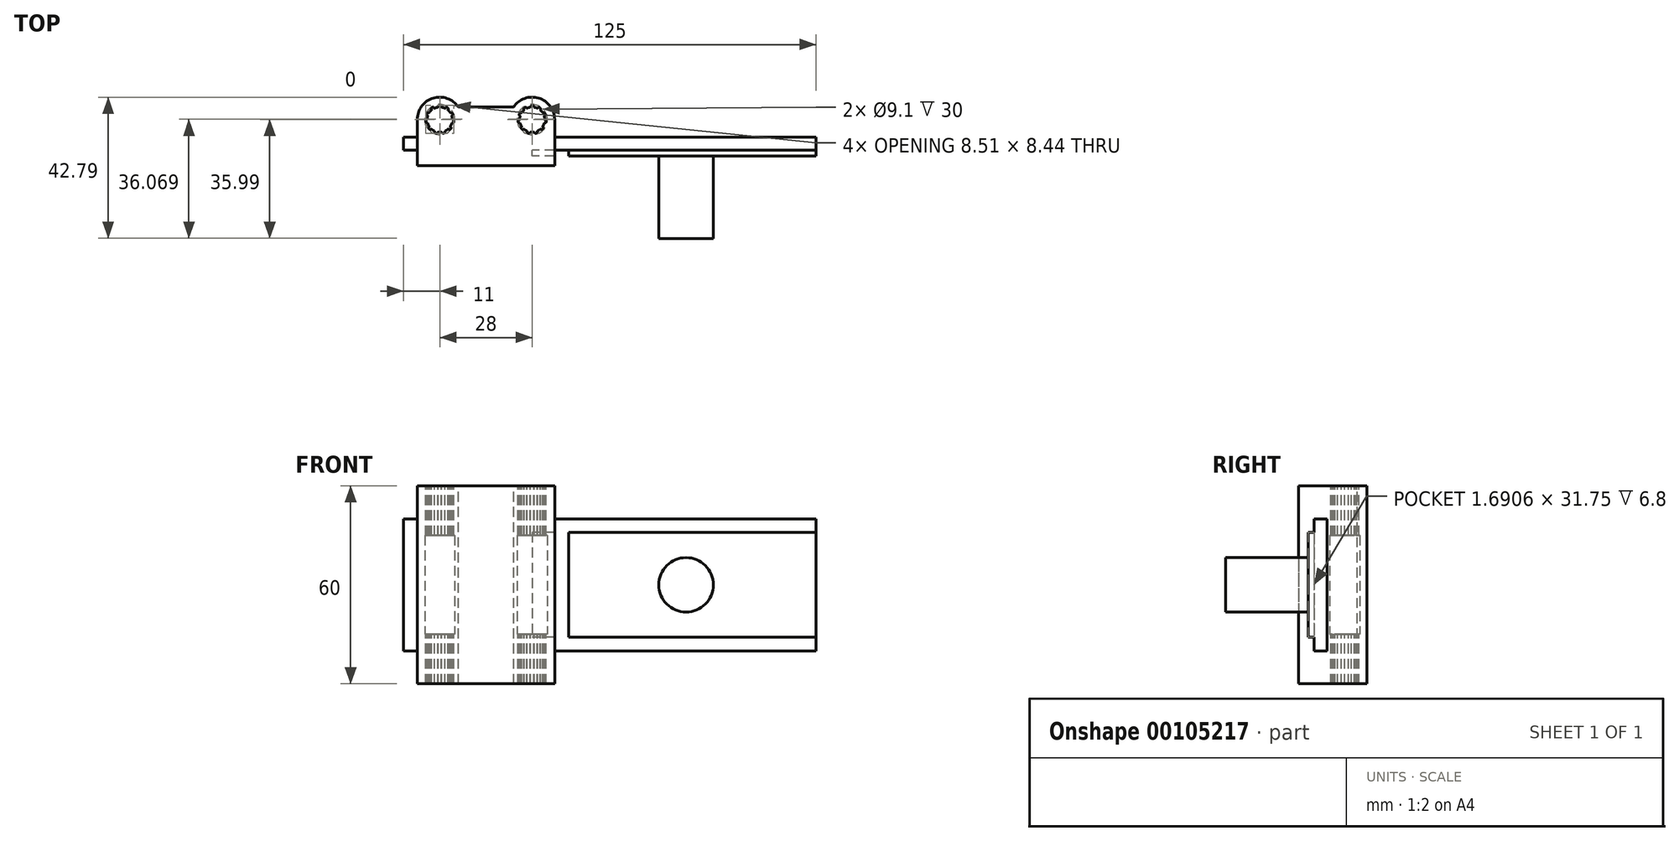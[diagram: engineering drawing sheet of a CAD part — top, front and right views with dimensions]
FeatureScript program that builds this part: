
annotation { "Feature Type Name" : "Feature", "Feature Type Description" : "" }
export const myFeature = defineFeature(function(context is Context, id is Id, definition is map)
    precondition{}
    {
        {
            assignVariable(context, id + "F0", {"name" : "tubeSpacing", "anyValue" : 28});
        }
        {
            var Q0;
            Q0=qCreatedBy(makeId("Right.planeOp"),FACE);
            var sketch = newSketch(context, id + "F1", { "sketchPlane" : qUnion([Q0])});
            skLineSegment(sketch, "E0.bottom", {"start": v(2, 20) * mm, "end": v(-2, 20) * mm});
            skLineSegment(sketch, "E0.top", {"start": v(2, -20) * mm, "end": v(-2, -20) * mm});
            skLineSegment(sketch, "E0.left", {"start": v(2, 20) * mm, "end": v(2, -20) * mm});
            skLineSegment(sketch, "E0.right", {"start": v(-2, 20) * mm, "end": v(-2, -20) * mm});
            skPoint(sketch, "E0.middle", {"position": v(0, 0) * mm});
            skLineSegment(sketch, "E1.bottom", {"start": v(-6, -28) * mm, "end": v(-2, -28) * mm});
            skLineSegment(sketch, "E1.top", {"start": v(-6, 28) * mm, "end": v(-2, 28) * mm});
            skLineSegment(sketch, "E1.left", {"start": v(-6, -28) * mm, "end": v(-6, 28) * mm});
            skPoint(sketch, "E1.middle", {"position": v(-4, 0) * mm});
            skLineSegment(sketch, "E2.bottom", {"start": v(6, -28) * mm, "end": v(2, -28) * mm});
            skLineSegment(sketch, "E2.top", {"start": v(6, 28) * mm, "end": v(2, 28) * mm});
            skLineSegment(sketch, "E2.left", {"start": v(6, -28) * mm, "end": v(6, 28) * mm});
            skPoint(sketch, "E2.middle", {"position": v(4, 0) * mm});
            skLineSegment(sketch, "E3", {"start": v(-2, 28) * mm, "end": v(2, 28) * mm});
            skLineSegment(sketch, "E4", {"start": v(-2, -28) * mm, "end": v(2, -28) * mm});
            skLineSegment(sketch, "E5", {"start": v(-2, 20) * mm, "end": v(-2, 28) * mm});
            skLineSegment(sketch, "E6", {"start": v(2, 20) * mm, "end": v(2, 28) * mm});
            skLineSegment(sketch, "E7", {"start": v(2, -20) * mm, "end": v(2, -28) * mm});
            skLineSegment(sketch, "E8", {"start": v(-2, -20) * mm, "end": v(-2, -28) * mm});
            skPoint(sketch, "E9", {"position": v(0, 24) * mm});
            skPoint(sketch, "E9.positionSnap0", {"position": v(-2, 24) * mm});
            skPoint(sketch, "E9.positionSnap1", {"position": v(0, 20) * mm});
            skPoint(sketch, "E10", {"position": v(0, -24) * mm});
            skLineSegment(sketch, "E11.bottom", {"start": v(-2.5, -15.88) * mm, "end": v(-3.7, -15.88) * mm});
            skLineSegment(sketch, "E11.top", {"start": v(-2.5, 15.88) * mm, "end": v(-3.7, 15.88) * mm});
            skLineSegment(sketch, "E11.left", {"start": v(-2.5, -15.88) * mm, "end": v(-2.5, 15.88) * mm});
            skLineSegment(sketch, "E11.right", {"start": v(-3.7, -15.88) * mm, "end": v(-3.7, 15.88) * mm});
            skPoint(sketch, "E11.middle", {"position": v(-3.1, 0) * mm});
            skLineSegment(sketch, "E12", {"start": v(-2.5, 15.88) * mm, "end": v(-2, 15.88) * mm});
            skLineSegment(sketch, "E13", {"start": v(-2.5, -15.88) * mm, "end": v(-2, -15.88) * mm});
            skSolve(sketch);
        }
        {
            var Q0;
            {var subQ1=sQuery(id+"F1.wireOp",EDGE,"E0.bottom");Q0=makeQuery(id+"F1.imprint","IMPRINT",FACE,{"disambiguationData":[TD([[makeQuery(id+"F1.imprint","IMPRINT",EDGE,{"derivedFrom":subQ1}),1.0]])]});}
            extrude(context, id + "F2", {"entities" : qUnion([Q0]), "oppositeDirection" : true, "depth" : 25 * mm, "hasSecondDirection" : true, "secondDirectionOppositeDirection" : false, "secondDirectionDepth" : 100 * mm});
        }
        {
            var Q0;
            Q0=makeQuery(id+"F1.imprint","IMPRINT",FACE,{"disambiguationData":[TD([[makeQuery(id+"F1.imprint","IMPRINT",EDGE,{"derivedFrom":sQuery(id+"F1.wireOp",EDGE,"E11.bottom")}),-1.0]])]});
            var Q1;
            Q1=makeQuery(id+"F1.imprint","IMPRINT",FACE,{"disambiguationData":[TD([[makeQuery(id+"F1.imprint","IMPRINT",EDGE,{"derivedFrom":sQuery(id+"F1.wireOp",EDGE,"E11.left")}),-1.0]])]});
            extrude(context, id + "F3", {"entities" : qUnion([Q0, Q1]), "operationType" : NewBodyOperationType.ADD, "depth" : 100 * mm, "hasSecondDirection" : true, "secondDirectionOppositeDirection" : false, "secondDirectionDepth" : (getVariable(context, 'tubeSpacing') / 2) * mm});
        }
        {
            var Q0;
            Q0=qCreatedBy(makeId("Top.planeOp"),FACE);
            var sketch = newSketch(context, id + "F4", { "sketchPlane" : qUnion([Q0])});
            skArc(sketch, "E14", {"start": v(-16.46, 10.2) * mm, "mid": v(-16.87, 9.79) * mm, "end": v(-17.22, 9.32) * mm});
            skLineSegment(sketch, "E15", {"start": v(-14, 7.3) * mm, "end": v(14, 7.3) * mm, "construction": true});
            skPoint(sketch, "E16", {"position": v(0, 7.3) * mm});
            skArc(sketch, "E17", {"start": v(-9.74, 2) * mm, "mid": v(-11.06, 13.43) * mm, "end": v(-20.8, 7.3) * mm});
            skArc(sketch, "E18", {"start": v(20.8, 7.3) * mm, "mid": v(11.06, 13.43) * mm, "end": v(9.74, 2) * mm});
            skLineSegment(sketch, "E19.0.0", {"start": v(100, -2) * mm, "end": v(100, 2) * mm});
            skLineSegment(sketch, "E19.0.1", {"start": v(100, 2) * mm, "end": v(-25, 2) * mm});
            skLineSegment(sketch, "E19.0.2", {"start": v(-25, 2) * mm, "end": v(-25, -2) * mm});
            skLineSegment(sketch, "E19.0.3", {"start": v(-25, -2) * mm, "end": v(100, -2) * mm});
            skLineSegment(sketch, "E20", {"start": v(-14, 11.1) * mm, "end": v(-8.36, 11.1) * mm, "construction": true});
            skLineSegment(sketch, "E21", {"start": v(-8.36, 11.1) * mm, "end": v(8.36, 11.1) * mm});
            skLineSegment(sketch, "E22", {"start": v(8.36, 11.1) * mm, "end": v(14, 11.1) * mm, "construction": true});
            skLineSegment(sketch, "E23", {"start": v(-20.8, 2) * mm, "end": v(-20.8, 7.3) * mm});
            skLineSegment(sketch, "E24", {"start": v(0, 7.3) * mm, "end": v(0, 0) * mm, "construction": true});
            skLineSegment(sketch, "E25.MirrorCS", {"start": v(20.8, 2) * mm, "end": v(20.8, 7.3) * mm});
            skCircle(sketch, "E26", {"center": v(-14, 7.3) * mm, "radius": 4.55 * mm});
            skCircle(sketch, "E27", {"center": v(14, 7.3) * mm, "radius": 4.55 * mm});
            skArc(sketch, "E28", {"start": v(-13.5, 11.07) * mm, "mid": v(-14, 11.6) * mm, "end": v(-14.5, 11.07) * mm});
            skArc(sketch, "E29.1.0", {"start": v(-15.62, 10.74) * mm, "mid": v(-16.32, 10.92) * mm, "end": v(-16.46, 10.2) * mm});
            skArc(sketch, "E29.2.0", {"start": v(-17.22, 9.32) * mm, "mid": v(-17.91, 9.09) * mm, "end": v(-17.63, 8.41) * mm});
            skArc(sketch, "E29.3.0", {"start": v(-17.8, 7.26) * mm, "mid": v(-18.26, 6.69) * mm, "end": v(-17.66, 6.27) * mm});
            skArc(sketch, "E29.4.0", {"start": v(-17.17, 5.21) * mm, "mid": v(-17.25, 4.48) * mm, "end": v(-16.52, 4.46) * mm});
            skArc(sketch, "E29.5.0", {"start": v(-15.54, 3.83) * mm, "mid": v(-15.21, 3.17) * mm, "end": v(-14.58, 3.54) * mm});
            skArc(sketch, "E29.6.0", {"start": v(-13.42, 3.54) * mm, "mid": v(-12.79, 3.17) * mm, "end": v(-12.46, 3.83) * mm});
            skArc(sketch, "E29.7.0", {"start": v(-11.48, 4.46) * mm, "mid": v(-10.75, 4.48) * mm, "end": v(-10.83, 5.21) * mm});
            skArc(sketch, "E29.8.0", {"start": v(-10.34, 6.27) * mm, "mid": v(-9.74, 6.69) * mm, "end": v(-10.2, 7.26) * mm});
            skArc(sketch, "E29.9.0", {"start": v(-10.37, 8.41) * mm, "mid": v(-10.09, 9.09) * mm, "end": v(-10.78, 9.32) * mm});
            skArc(sketch, "E29.10.0", {"start": v(-11.54, 10.2) * mm, "mid": v(-11.68, 10.92) * mm, "end": v(-12.38, 10.74) * mm});
            skArc(sketch, "E30.trimOffspring", {"start": v(-14.5, 11.07) * mm, "mid": v(-15.07, 10.95) * mm, "end": v(-15.62, 10.74) * mm});
            skArc(sketch, "E31.trimOffspring", {"start": v(-12.38, 10.74) * mm, "mid": v(-12.93, 10.95) * mm, "end": v(-13.5, 11.07) * mm});
            skArc(sketch, "E32.trimOffspring", {"start": v(-10.78, 9.32) * mm, "mid": v(-11.13, 9.79) * mm, "end": v(-11.54, 10.2) * mm});
            skArc(sketch, "E33.trimOffspring", {"start": v(-10.2, 7.26) * mm, "mid": v(-10.24, 7.84) * mm, "end": v(-10.37, 8.41) * mm});
            skArc(sketch, "E34.trimOffspring", {"start": v(-10.83, 5.21) * mm, "mid": v(-10.54, 5.72) * mm, "end": v(-10.34, 6.27) * mm});
            skArc(sketch, "E35.trimOffspring", {"start": v(-12.46, 3.83) * mm, "mid": v(-11.95, 4.1) * mm, "end": v(-11.48, 4.46) * mm});
            skArc(sketch, "E36.trimOffspring", {"start": v(-14.58, 3.54) * mm, "mid": v(-14, 3.5) * mm, "end": v(-13.42, 3.54) * mm});
            skArc(sketch, "E37.trimOffspring", {"start": v(-16.52, 4.46) * mm, "mid": v(-16.05, 4.1) * mm, "end": v(-15.54, 3.83) * mm});
            skArc(sketch, "E38.trimOffspring", {"start": v(-17.66, 6.27) * mm, "mid": v(-17.46, 5.72) * mm, "end": v(-17.17, 5.21) * mm});
            skArc(sketch, "E39.trimOffspring", {"start": v(-17.63, 8.41) * mm, "mid": v(-17.76, 7.84) * mm, "end": v(-17.8, 7.26) * mm});
            skArc(sketch, "E40.MirrorCS", {"start": v(13.5, 11.07) * mm, "mid": v(14, 11.6) * mm, "end": v(14.5, 11.07) * mm});
            skArc(sketch, "E41.MirrorCS", {"start": v(12.38, 10.74) * mm, "mid": v(12.93, 10.95) * mm, "end": v(13.5, 11.07) * mm});
            skArc(sketch, "E42.MirrorCS", {"start": v(11.54, 10.2) * mm, "mid": v(11.68, 10.92) * mm, "end": v(12.38, 10.74) * mm});
            skArc(sketch, "E43.MirrorCS", {"start": v(10.78, 9.32) * mm, "mid": v(11.13, 9.79) * mm, "end": v(11.54, 10.2) * mm});
            skArc(sketch, "E44.MirrorCS", {"start": v(10.37, 8.41) * mm, "mid": v(10.09, 9.09) * mm, "end": v(10.78, 9.32) * mm});
            skArc(sketch, "E45.MirrorCS", {"start": v(10.2, 7.26) * mm, "mid": v(10.24, 7.84) * mm, "end": v(10.37, 8.41) * mm});
            skArc(sketch, "E46.MirrorCS", {"start": v(10.34, 6.27) * mm, "mid": v(9.74, 6.69) * mm, "end": v(10.2, 7.26) * mm});
            skArc(sketch, "E47.MirrorCS", {"start": v(10.83, 5.21) * mm, "mid": v(10.54, 5.72) * mm, "end": v(10.34, 6.27) * mm});
            skArc(sketch, "E48.MirrorCS", {"start": v(11.48, 4.46) * mm, "mid": v(10.75, 4.48) * mm, "end": v(10.83, 5.21) * mm});
            skArc(sketch, "E49.MirrorCS", {"start": v(12.46, 3.83) * mm, "mid": v(11.95, 4.1) * mm, "end": v(11.48, 4.46) * mm});
            skArc(sketch, "E50.MirrorCS", {"start": v(13.42, 3.54) * mm, "mid": v(12.79, 3.17) * mm, "end": v(12.46, 3.83) * mm});
            skArc(sketch, "E51.MirrorCS", {"start": v(14.58, 3.54) * mm, "mid": v(14, 3.5) * mm, "end": v(13.42, 3.54) * mm});
            skArc(sketch, "E52.MirrorCS", {"start": v(15.54, 3.83) * mm, "mid": v(15.21, 3.17) * mm, "end": v(14.58, 3.54) * mm});
            skArc(sketch, "E53.MirrorCS", {"start": v(16.52, 4.46) * mm, "mid": v(16.05, 4.1) * mm, "end": v(15.54, 3.83) * mm});
            skArc(sketch, "E54.MirrorCS", {"start": v(17.17, 5.21) * mm, "mid": v(17.25, 4.48) * mm, "end": v(16.52, 4.46) * mm});
            skArc(sketch, "E55.MirrorCS", {"start": v(17.66, 6.27) * mm, "mid": v(17.46, 5.72) * mm, "end": v(17.17, 5.21) * mm});
            skArc(sketch, "E56.MirrorCS", {"start": v(17.8, 7.26) * mm, "mid": v(18.26, 6.69) * mm, "end": v(17.66, 6.27) * mm});
            skArc(sketch, "E57.MirrorCS", {"start": v(17.63, 8.41) * mm, "mid": v(17.76, 7.84) * mm, "end": v(17.8, 7.26) * mm});
            skArc(sketch, "E58.MirrorCS", {"start": v(17.22, 9.32) * mm, "mid": v(17.91, 9.09) * mm, "end": v(17.63, 8.41) * mm});
            skArc(sketch, "E59.MirrorCS", {"start": v(16.46, 10.2) * mm, "mid": v(16.87, 9.79) * mm, "end": v(17.22, 9.32) * mm});
            skArc(sketch, "E60.MirrorCS", {"start": v(15.62, 10.74) * mm, "mid": v(16.32, 10.92) * mm, "end": v(16.46, 10.2) * mm});
            skArc(sketch, "E61.MirrorCS", {"start": v(14.5, 11.07) * mm, "mid": v(15.07, 10.95) * mm, "end": v(15.62, 10.74) * mm});
            skSolve(sketch);
        }
        {
            var Q0;
            {var subQ0=sQuery(id+"F4.wireOp",EDGE,"E23");Q0=makeQuery(id+"F4.imprint","IMPRINT",FACE,{"disambiguationData":[TD([[makeQuery(id+"F4.imprint","IMPRINT",EDGE,{"derivedFrom":subQ0}),-1.0]])]});}
            var Q1;
            Q1=makeQuery(id+"F4.imprint","IMPRINT",FACE,{"disambiguationData":[TD([[makeQuery(id+"F4.imprint","IMPRINT",EDGE,{"derivedFrom":sQuery(id+"F4.wireOp",EDGE,"E14")}),-1.0]])]});
            var Q2;
            {var subQ3=sQuery(id+"F4.wireOp",EDGE,"E21");Q2=makeQuery(id+"F4.imprint","IMPRINT",FACE,{"disambiguationData":[TD([[makeQuery(id+"F4.imprint","IMPRINT",EDGE,{"derivedFrom":subQ3}),-1.0]])]});}
            var Q3;
            {var subQ0=sQuery(id+"F4.wireOp",EDGE,"E25.MirrorCS");Q3=makeQuery(id+"F4.imprint","IMPRINT",FACE,{"disambiguationData":[TD([[makeQuery(id+"F4.imprint","IMPRINT",EDGE,{"derivedFrom":subQ0}),1.0]])]});}
            var Q4;
            Q4=makeQuery(id+"F4.imprint","IMPRINT",FACE,{"disambiguationData":[TD([[makeQuery(id+"F4.imprint","IMPRINT",EDGE,{"derivedFrom":sQuery(id+"F4.wireOp",EDGE,"xitLeMhD-En1o-M4un-lO6Y-eS4zLTXDa6B0")}),-1.0]])]});
            var Q5;
            Q5=makeQuery(id+"F4.imprint","IMPRINT",FACE,{"disambiguationData":[TD([[makeQuery(id+"F4.imprint","IMPRINT",EDGE,{"derivedFrom":sQuery(id+"F4.wireOp",EDGE,"E27")}),1.0]])]});
            extrude(context, id + "F5", {"entities" : qUnion([Q0, Q1, Q2, Q3, Q4, Q5]), "oppositeDirection" : true, "depth" : 30 * mm, "hasSecondDirection" : true, "secondDirectionOppositeDirection" : false, "secondDirectionDepth" : 30 * mm});
        }
        {
            var Q0;
            Q0=makeQuery(id+"F4.imprint","IMPRINT",FACE,{"disambiguationData":[TD([[makeQuery(id+"F4.imprint","IMPRINT",EDGE,{"derivedFrom":sQuery(id+"F4.wireOp",EDGE,"E14")}),-1.0]])]});
            var Q1;
            Q1=makeQuery(id+"F4.imprint","IMPRINT",FACE,{"disambiguationData":[TD([[makeQuery(id+"F4.imprint","IMPRINT",EDGE,{"derivedFrom":sQuery(id+"F4.wireOp",EDGE,"xitLeMhD-En1o-M4un-lO6Y-eS4zLTXDa6B0")}),-1.0]])]});
            var Q2;
            Q2=makeQuery(id+"F4.imprint","IMPRINT",FACE,{"disambiguationData":[TD([[makeQuery(id+"F4.imprint","IMPRINT",EDGE,{"derivedFrom":sQuery(id+"F4.wireOp",EDGE,"E27")}),1.0]])]});
            var Q3;
            Q3=makeQuery(id+"F4.imprint","IMPRINT",FACE,{"disambiguationData":[TD([[makeQuery(id+"F4.imprint","IMPRINT",EDGE,{"derivedFrom":sQuery(id+"F4.wireOp",EDGE,"E40.MirrorCS")}),-1.0]])]});
            extrude(context, id + "F6", {"entities" : qUnion([Q0, Q1, Q2, Q3]), "operationType" : NewBodyOperationType.REMOVE, "depth" : 15 * mm, "hasSecondDirection" : true, "secondDirectionOppositeDirection" : true, "secondDirectionDepth" : 15 * mm});
        }
        {
            var Q0;
            Q0=makeQuery(id+"F5.opExtrude","SWEPT_FACE",FACE,{"disambiguationData":[OSD([sQuery(id+"F4.wireOp",EDGE,"E19.0.1")])]});
            var sketch = newSketch(context, id + "F7", { "sketchPlane" : qUnion([Q0])});
            skLineSegment(sketch, "E62.0", {"start": v(-20.8, -20) * mm, "end": v(20.8, -20) * mm});
            skLineSegment(sketch, "E63.0", {"start": v(-20.8, 20) * mm, "end": v(20.8, 20) * mm});
            skLineSegment(sketch, "E64.0", {"start": v(-20.8, -30) * mm, "end": v(-20.8, 30) * mm});
            skLineSegment(sketch, "E65.0", {"start": v(20.8, -30) * mm, "end": v(20.8, 30) * mm});
            skLineSegment(sketch, "E66.0", {"start": v(20.8, -30) * mm, "end": v(-20.8, -30) * mm});
            skLineSegment(sketch, "E67.0", {"start": v(20.8, 30) * mm, "end": v(-20.8, 30) * mm});
            skPoint(sketch, "E68.0", {"position": v(-14, 0) * mm});
            skPoint(sketch, "E69.0", {"position": v(14, 0) * mm});
            skLineSegment(sketch, "E70", {"start": v(-14, -30) * mm, "end": v(-14, 30) * mm, "construction": true});
            skLineSegment(sketch, "E71", {"start": v(14, -30) * mm, "end": v(14, 30) * mm, "construction": true});
            skSolve(sketch);
        }
        {
            var Q0;
            {var subQ0=sQuery(id+"F7.wireOp",EDGE,"E62.0");Q0=makeQuery(id+"F7.imprint","IMPRINT",FACE,{"disambiguationData":[TD([[makeQuery(id+"F7.imprint","IMPRINT",EDGE,{"derivedFrom":subQ0}),-1.0]])]});}
            extrude(context, id + "F8", {"entities" : qUnion([Q0]), "operationType" : NewBodyOperationType.ADD, "depth" : 4 * mm});
        }
        {
            var Q0;
            Q0=qCreatedBy(makeId("Top.planeOp"),FACE);
            var sketch = newSketch(context, id + "F9", { "sketchPlane" : qUnion([Q0])});
            skLineSegment(sketch, "E72.0", {"start": v(-20.8, 2) * mm, "end": v(-20.8, 7.3) * mm, "construction": true});
            skLineSegment(sketch, "E73.0", {"start": v(20.8, 2) * mm, "end": v(20.8, 7.3) * mm, "construction": true});
            skLineSegment(sketch, "E74.0", {"start": v(-25, -2) * mm, "end": v(100, -2) * mm, "construction": true});
            skPoint(sketch, "E75.0", {"position": v(14, 7.3) * mm});
            skPoint(sketch, "E76.0", {"position": v(-14, 7.3) * mm});
            skLineSegment(sketch, "E77", {"start": v(-20.8, -2) * mm, "end": v(-20.8, -6.7) * mm});
            skLineSegment(sketch, "E78", {"start": v(20.8, -2) * mm, "end": v(20.8, -6.7) * mm});
            skLineSegment(sketch, "E79", {"start": v(20.8, -6.7) * mm, "end": v(-20.8, -6.7) * mm});
            skLineSegment(sketch, "E80", {"start": v(-20.8, -2) * mm, "end": v(20.8, -2) * mm});
            skLineSegment(sketch, "E81.0", {"start": v(100, -3.7) * mm, "end": v(14, -3.7) * mm, "construction": true});
            skSolve(sketch);
        }
        {
            var Q0;
            Q0=makeQuery(id+"F9.imprint","IMPRINT",FACE,{"disambiguationData":[TD([[makeQuery(id+"F9.imprint","IMPRINT",EDGE,{"derivedFrom":sQuery(id+"F9.wireOp",EDGE,"E77")}),1.0]])]});
            extrude(context, id + "F10", {"entities" : qUnion([Q0]), "depth" : 30 * mm, "hasSecondDirection" : true, "secondDirectionOppositeDirection" : true, "secondDirectionDepth" : 30 * mm});
        }
        {
            var Q0;
            {var subQ0=sQuery(id+"F7.wireOp",EDGE,"E63.0");Q0=makeQuery(id+"F7.imprint","IMPRINT",FACE,{"disambiguationData":[TD([[makeQuery(id+"F7.imprint","IMPRINT",EDGE,{"derivedFrom":subQ0}),1.0]])]});}
            var Q1;
            Q1=makeQuery(id+"F10.opExtrude","SWEPT_BODY",BODY,{"disambiguationData":[OSD([sQuery(id+"F9.wireOp",EDGE,"E77"),sQuery(id+"F9.wireOp",EDGE,"E78"),sQuery(id+"F9.wireOp",EDGE,"E79"),sQuery(id+"F9.wireOp",EDGE,"E80")])]});
            extrude(context, id + "F11", {"entities" : qUnion([Q0]), "operationType" : NewBodyOperationType.ADD, "endBound" : BoundingType.UP_TO_BODY, "endBoundEntityBody" : qUnion([Q1]), "depth" : 25 * mm});
        }
        {
            var Q0;
            Q0=makeQuery(id+"F1.imprint","IMPRINT",FACE,{"disambiguationData":[TD([[makeQuery(id+"F1.imprint","IMPRINT",EDGE,{"derivedFrom":sQuery(id+"F1.wireOp",EDGE,"E11.left")}),-1.0]])]});
            var Q1;
            Q1=makeQuery(id+"F1.imprint","IMPRINT",FACE,{"disambiguationData":[TD([[makeQuery(id+"F1.imprint","IMPRINT",EDGE,{"derivedFrom":sQuery(id+"F1.wireOp",EDGE,"E11.bottom")}),-1.0]])]});
            extrude(context, id + "F12", {"entities" : qUnion([Q0, Q1]), "operationType" : NewBodyOperationType.REMOVE, "depth" : 25 * mm, "hasSecondDirection" : true, "secondDirectionOppositeDirection" : false, "secondDirectionDepth" : (getVariable(context, 'tubeSpacing') / 2) * mm});
        }
        {
            var Q0;
            Q0=makeQuery(id+"F3.opExtrude","SWEPT_FACE",FACE,{"disambiguationData":[OSD([sQuery(id+"F1.wireOp",EDGE,"E11.right")])]});
            var sketch = newSketch(context, id + "F13", { "sketchPlane" : qUnion([Q0])});
            skCircle(sketch, "E82", {"center": v(60.61, 0) * mm, "radius": 8.27 * mm});
            skSolve(sketch);
        }
        {
            var Q0;
            Q0=makeQuery(id+"F13.imprint","IMPRINT",FACE,{"disambiguationData":[TD([[makeQuery(id+"F13.imprint","IMPRINT",EDGE,{"derivedFrom":sQuery(id+"F13.wireOp",EDGE,"E82")}),1.0]])]});
            extrude(context, id + "F14", {"entities" : qUnion([Q0]), "operationType" : NewBodyOperationType.ADD, "depth" : 25 * mm});
        }
    });
